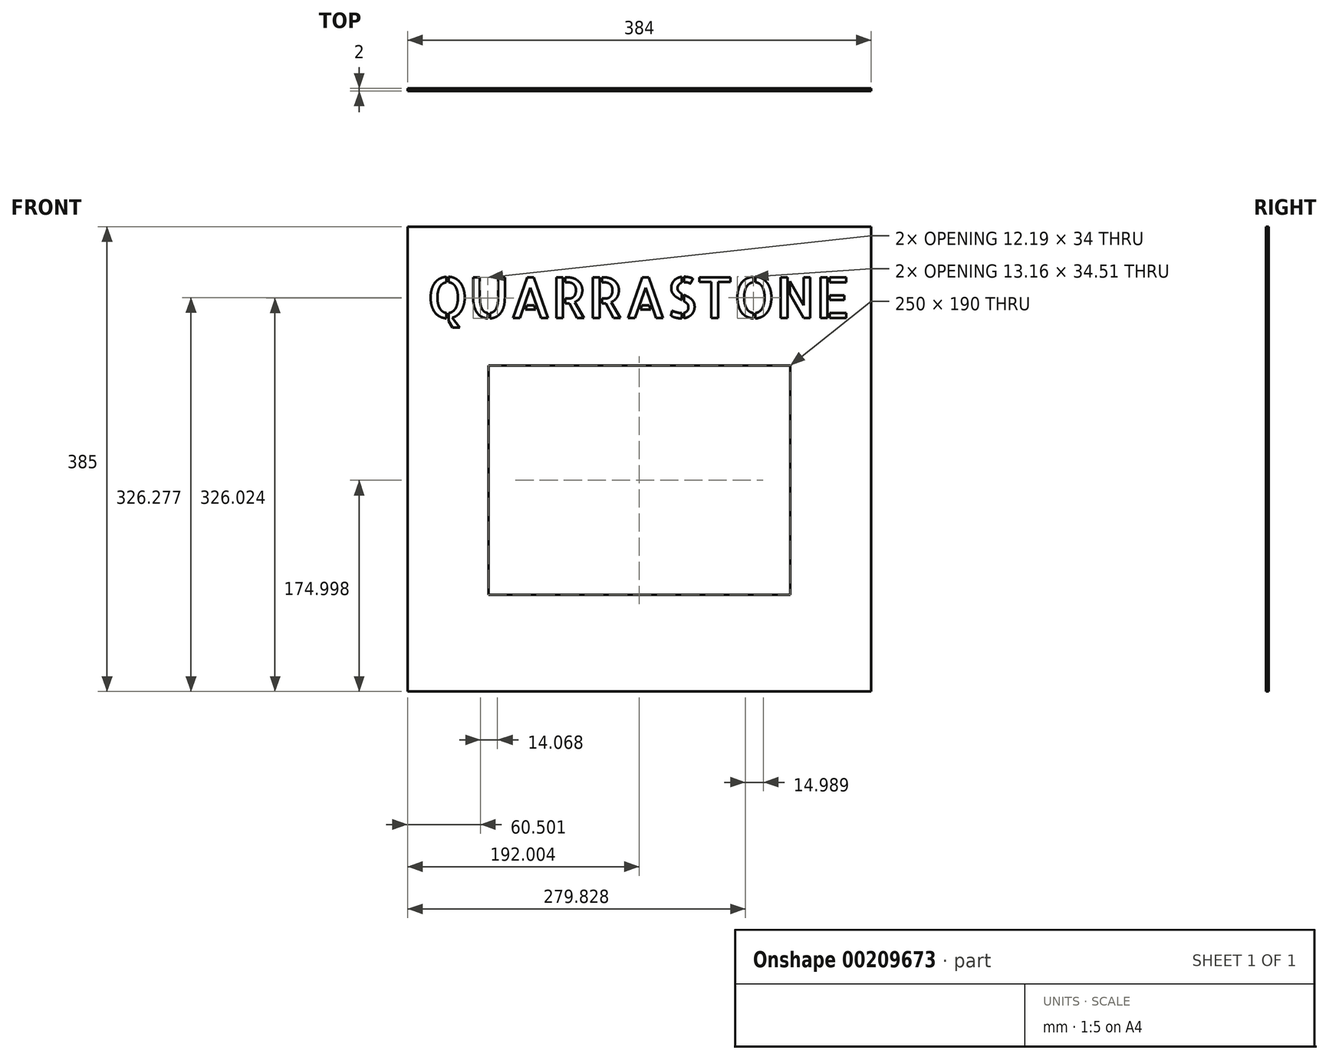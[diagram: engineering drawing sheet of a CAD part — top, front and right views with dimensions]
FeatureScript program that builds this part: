
annotation { "Feature Type Name" : "Feature", "Feature Type Description" : "" }
export const myFeature = defineFeature(function(context is Context, id is Id, definition is map)
    precondition{}
    {
        {
            var Q0;
            Q0=qCreatedBy(makeId("Front.planeOp"),FACE);
            var sketch = newSketch(context, id + "F0", { "sketchPlane" : qUnion([Q0])});
            skLineSegment(sketch, "E0.bottom", {"start": v(-203.35, 236.48) * mm, "end": v(180.65, 236.48) * mm});
            skLineSegment(sketch, "E0.top", {"start": v(-203.35, -148.52) * mm, "end": v(180.65, -148.52) * mm});
            skLineSegment(sketch, "E0.left", {"start": v(-203.35, 236.48) * mm, "end": v(-203.35, -148.52) * mm});
            skLineSegment(sketch, "E0.right", {"start": v(180.65, 236.48) * mm, "end": v(180.65, -148.52) * mm});
            skPoint(sketch, "E1.positionSnap0", {"position": v(-203.35, 43.98) * mm});
            skPoint(sketch, "E1.positionSnap1", {"position": v(-11.35, 236.48) * mm});
            skLineSegment(sketch, "E2.bottom", {"start": v(113.65, -68.52) * mm, "end": v(-136.35, -68.52) * mm});
            skLineSegment(sketch, "E2.top", {"start": v(113.65, 121.48) * mm, "end": v(-136.35, 121.48) * mm});
            skLineSegment(sketch, "E2.left", {"start": v(113.65, -68.52) * mm, "end": v(113.65, 121.48) * mm});
            skLineSegment(sketch, "E2.right", {"start": v(-136.35, -68.52) * mm, "end": v(-136.35, 121.48) * mm});
            skText(sketch, "E3", { "text": "QUARRASTONE", "fontName": "AllertaStencil-Regular.ttf"});
            const initialGuessF0  = {"E3": [-0.18703, 0.16073, 1, 0, 0.03379]};
            skSetInitialGuess(sketch, initialGuessF0);
            skSolve(sketch);
        }
        {
            var Q0;
            Q0=makeQuery(id+"F0.imprint","IMPRINT",FACE,{"disambiguationData":[TD([[makeQuery(id+"F0.imprint","IMPRINT",EDGE,{"derivedFrom":sQuery(id+"F0.wireOp",EDGE,"E0.bottom")}),-1.0]])]});
            extrude(context, id + "F1", {"entities" : qUnion([Q0]), "depth" : 2 * mm});
        }
    });
